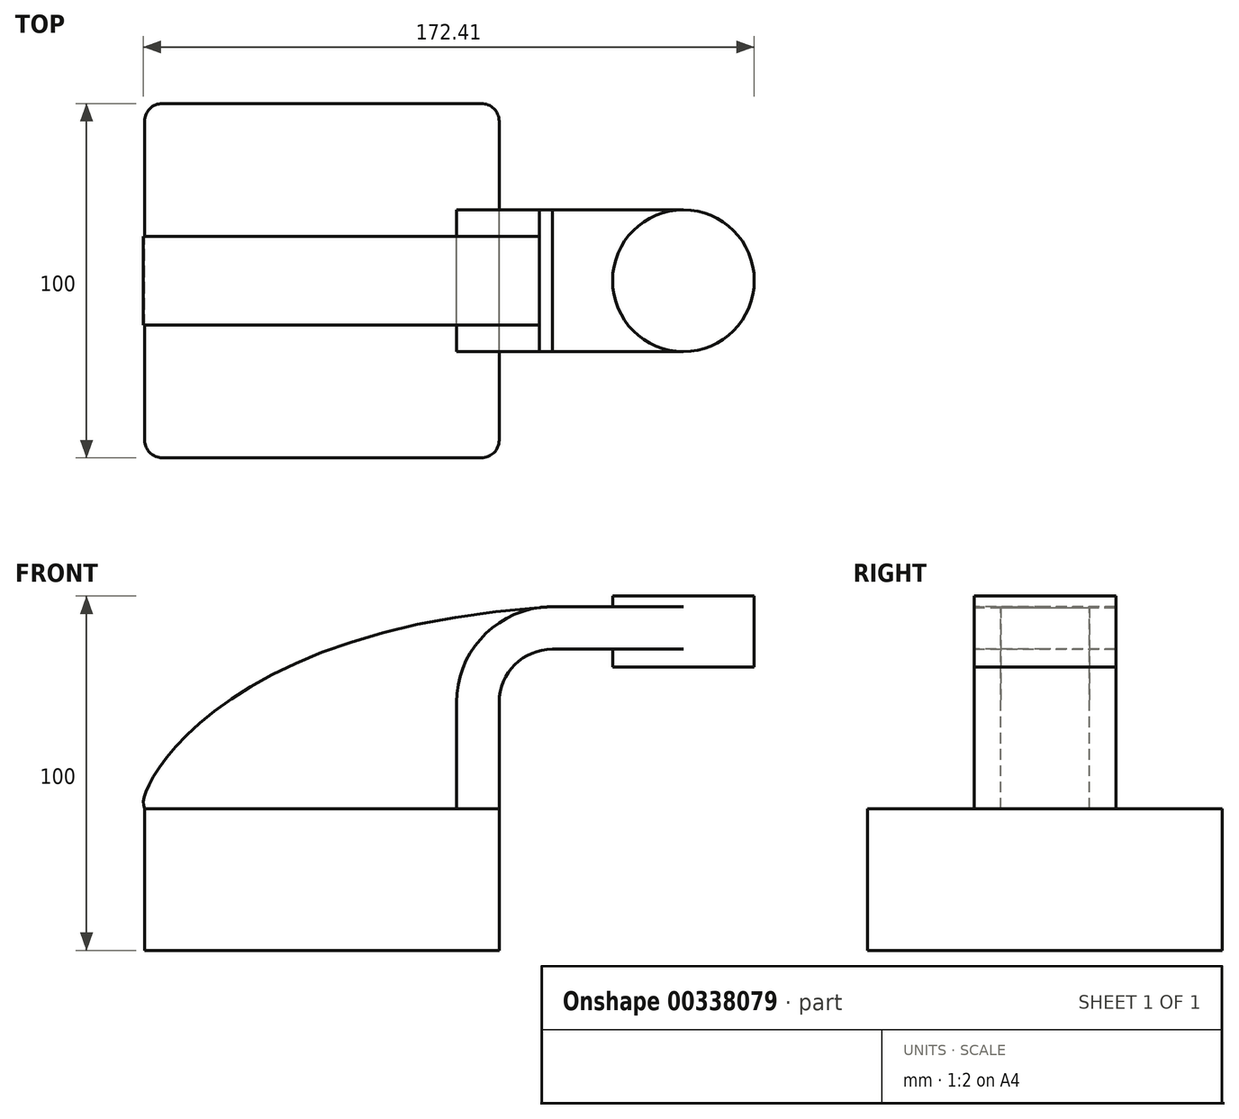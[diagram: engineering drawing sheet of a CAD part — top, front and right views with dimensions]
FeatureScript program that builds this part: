
annotation { "Feature Type Name" : "Feature", "Feature Type Description" : "" }
export const myFeature = defineFeature(function(context is Context, id is Id, definition is map)
    precondition{}
    {
        {
            var Q0;
            Q0=qCreatedBy(makeId("Front.planeOp"),FACE);
            var sketch = newSketch(context, id + "F0", { "sketchPlane" : qUnion([Q0])});
            skLineSegment(sketch, "E0.bottom", {"start": v(-50, 20) * mm, "end": v(50, 20) * mm});
            skLineSegment(sketch, "E0.top", {"start": v(-50, -20) * mm, "end": v(50, -20) * mm});
            skLineSegment(sketch, "E0.left", {"start": v(-50, 20) * mm, "end": v(-50, -20) * mm});
            skLineSegment(sketch, "E0.right", {"start": v(50, 20) * mm, "end": v(50, -20) * mm});
            skPoint(sketch, "E0.middle", {"position": v(0, 0) * mm});
            skLineSegment(sketch, "E1.bottom", {"start": v(122, 60) * mm, "end": v(82, 60) * mm});
            skLineSegment(sketch, "E1.top", {"start": v(122, 80) * mm, "end": v(82, 80) * mm});
            skLineSegment(sketch, "E1.left", {"start": v(122, 60) * mm, "end": v(122, 80) * mm});
            skLineSegment(sketch, "E1.right", {"start": v(82, 60) * mm, "end": v(82, 80) * mm});
            skPoint(sketch, "E1.middle", {"position": v(102, 70) * mm});
            skLineSegment(sketch, "E2", {"start": v(50, 20) * mm, "end": v(50, 50) * mm});
            skArc(sketch, "E3", {"start": v(50, 50) * mm, "mid": v(54.4, 60.6) * mm, "end": v(65, 65) * mm});
            skLineSegment(sketch, "E4", {"start": v(65, 65) * mm, "end": v(102, 65) * mm});
            skLineSegment(sketch, "E5.0", {"start": v(65, 77) * mm, "end": v(102, 77) * mm});
            skArc(sketch, "E5.1", {"start": v(38, 50) * mm, "mid": v(45.9, 69.1) * mm, "end": v(65, 77) * mm});
            skLineSegment(sketch, "E5.2", {"start": v(38, 20) * mm, "end": v(38, 50) * mm});
            skLineSegment(sketch, "E6", {"start": v(102, 60) * mm, "end": v(102, 80) * mm});
            skFitSpline(sketch, "E7", {"points": [v(-50, 20) * mm, v(-50, 23.89) * mm, v(65, 77) * mm], "startDerivative": vector(-10.08, 23.38) * mm, "endDerivative": vector(304.17, 18.8) * mm});
            skSolve(sketch);
        }
        {
            var Q0;
            Q0=makeQuery(id+"F0.imprint","IMPRINT",FACE,{"disambiguationData":[TD([[makeQuery(id+"F0.imprint","IMPRINT",EDGE,{"derivedFrom":sQuery(id+"F0.wireOp",EDGE,"E0.top")}),1.0]])]});
            extrude(context, id + "F1", {"entities" : qUnion([Q0]), "endBound" : BoundingType.SYMMETRIC, "depth" : 100 * mm});
        }
        {
            var Q0;
            {var subQ1=sQuery(id+"F0.wireOp",EDGE,"E2");Q0=makeQuery(id+"F0.imprint","IMPRINT",FACE,{"disambiguationData":[TD([[makeQuery(id+"F0.imprint","IMPRINT",EDGE,{"derivedFrom":subQ1}),1.0]])]});}
            var Q1;
            {var subQ0=sQuery(id+"F0.wireOp",EDGE,"E4");var subQ1=sQuery(id+"F0.wireOp",EDGE,"E1.right");var subQ2=makeQuery(id+"F0.imprint","INTERSECT",VERTEX,{"derivedFrom":[subQ1,subQ0]});Q1=makeQuery(id+"F0.imprint","IMPRINT",FACE,{"disambiguationData":[TD([[makeQuery(id+"F0.imprint","IMPRINT",EDGE,{"disambiguationData":[TD([[subQ2,-1.0]])],"derivedFrom":subQ1}),-1.0]])]});}
            extrude(context, id + "F2", {"entities" : qUnion([Q0, Q1]), "endBound" : BoundingType.SYMMETRIC, "depth" : 40 * mm});
        }
        {
            var Q0;
            {var subQ3=sQuery(id+"F0.wireOp",EDGE,"E5.2");Q0=makeQuery(id+"F0.imprint","IMPRINT",FACE,{"disambiguationData":[TD([[makeQuery(id+"F0.imprint","IMPRINT",EDGE,{"derivedFrom":subQ3}),1.0]])]});}
            extrude(context, id + "F3", {"entities" : qUnion([Q0]), "endBound" : BoundingType.SYMMETRIC, "depth" : 25 * mm});
        }
        {
            var Q0;
            {var subQ0=sQuery(id+"F0.wireOp",EDGE,"E1.left");Q0=makeQuery(id+"F0.imprint","IMPRINT",FACE,{"disambiguationData":[TD([[makeQuery(id+"F0.imprint","IMPRINT",EDGE,{"derivedFrom":subQ0}),1.0]])]});}
            var Q1;
            Q1=sQuery(id+"F0.wireOp",EDGE,"E6");
            revolve(context, id + "F4", {"operationType" : NewBodyOperationType.ADD, "entities" : qUnion([Q0]), "axis" : qUnion([Q1]), "revolveType" : RevolveType.FULL});
        }
        {
            var Q0;
            Q0=makeQuery(id+"F1.opExtrude","CAP_EDGE",EDGE,{"disambiguationData":[OSD([sQuery(id+"F0.wireOp",EDGE,"E0.left")])],"isStart":false});
            var Q1;
            Q1=makeQuery(id+"F1.opExtrude","CAP_EDGE",EDGE,{"disambiguationData":[OSD([sQuery(id+"F0.wireOp",EDGE,"E0.right")])],"isStart":false});
            var Q2;
            Q2=makeQuery(id+"F1.opExtrude","CAP_EDGE",EDGE,{"disambiguationData":[OSD([sQuery(id+"F0.wireOp",EDGE,"E0.right")])],"isStart":true});
            var Q3;
            Q3=makeQuery(id+"F1.opExtrude","CAP_EDGE",EDGE,{"disambiguationData":[OSD([sQuery(id+"F0.wireOp",EDGE,"E0.left")])],"isStart":true});
            fillet(context, id + "F5", {"entities" : qUnion([Q0, Q1, Q2, Q3]), "radius" : 5 * mm, "tangentPropagation" : true, "allowEdgeOverflow" : false});
        }
    });
